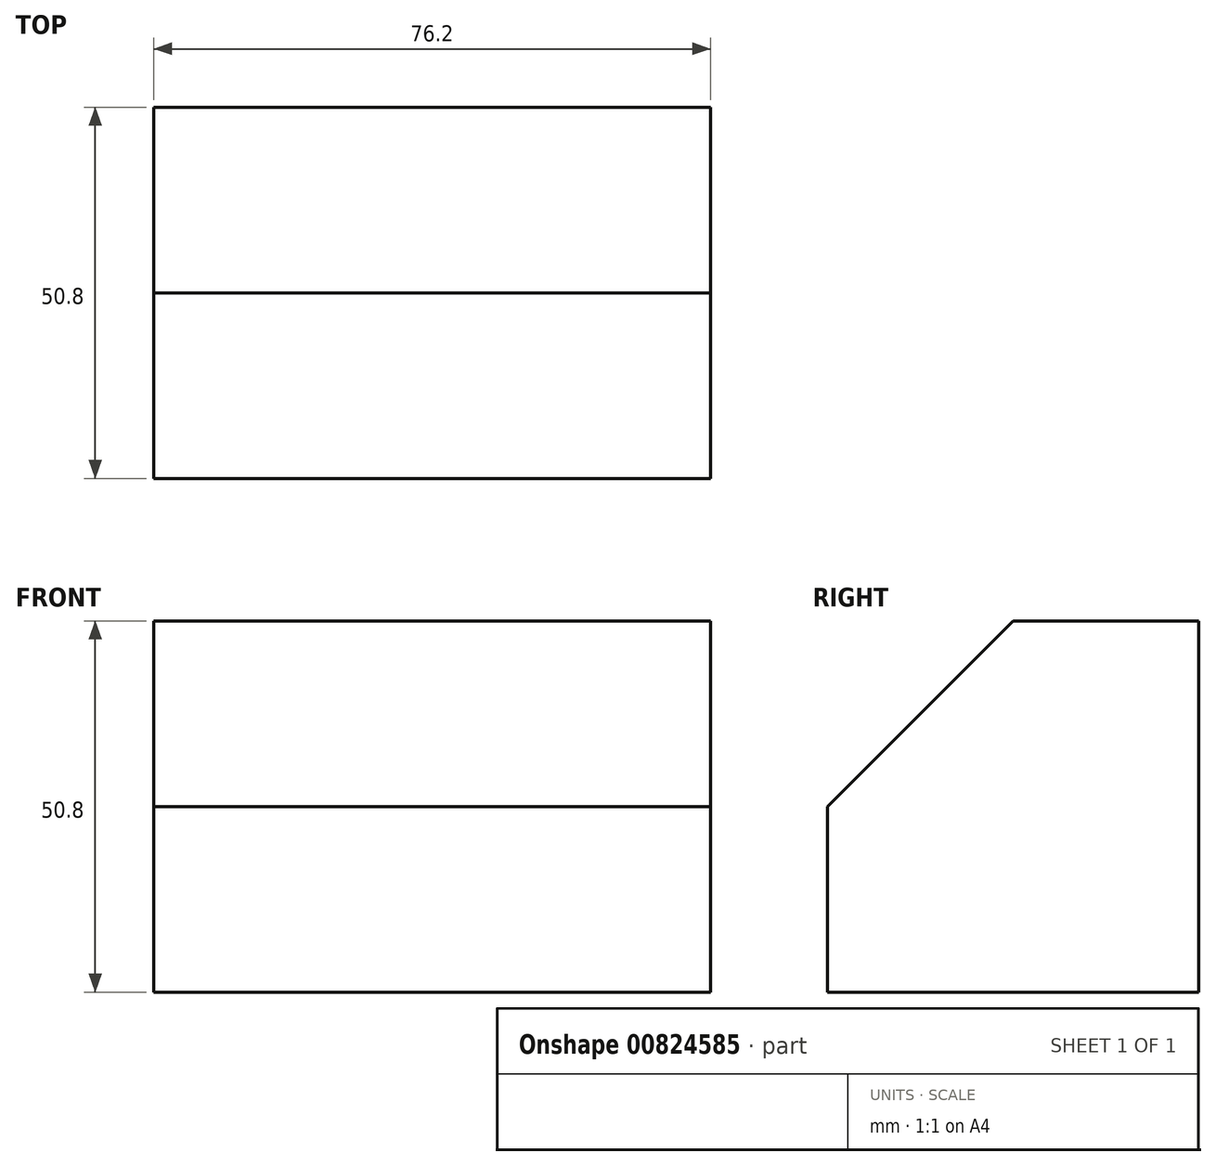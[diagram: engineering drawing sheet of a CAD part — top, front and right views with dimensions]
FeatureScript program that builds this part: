
annotation { "Feature Type Name" : "Feature", "Feature Type Description" : "" }
export const myFeature = defineFeature(function(context is Context, id is Id, definition is map)
    precondition{}
    {
        {
            var Q0;
            Q0=qCreatedBy(makeId("Right.planeOp"),FACE);
            var sketch = newSketch(context, id + "F0", { "sketchPlane" : qUnion([Q0])});
            skLineSegment(sketch, "E0", {"start": v(25.4, 0) * mm, "end": v(0, -25.4) * mm});
            skLineSegment(sketch, "E1", {"start": v(0, -50.8) * mm, "end": v(25.4, -50.8) * mm});
            skLineSegment(sketch, "E2", {"start": v(25.4, 0) * mm, "end": v(50.8, 0) * mm});
            skLineSegment(sketch, "E3", {"start": v(50.8, 0) * mm, "end": v(50.8, -50.8) * mm});
            skLineSegment(sketch, "E4", {"start": v(50.8, -50.8) * mm, "end": v(25.4, -50.8) * mm});
            skLineSegment(sketch, "E5", {"start": v(0, -25.4) * mm, "end": v(0, -50.8) * mm});
            skSolve(sketch);
        }
        {
            var Q0;
            Q0 = qSketchRegion(id + "F0", true);
            extrude(context, id + "F1", {"entities" : qUnion([Q0]), "depth" : 76.2 * mm, "offsetDistance" : 25.4 * mm});
        }
    });
